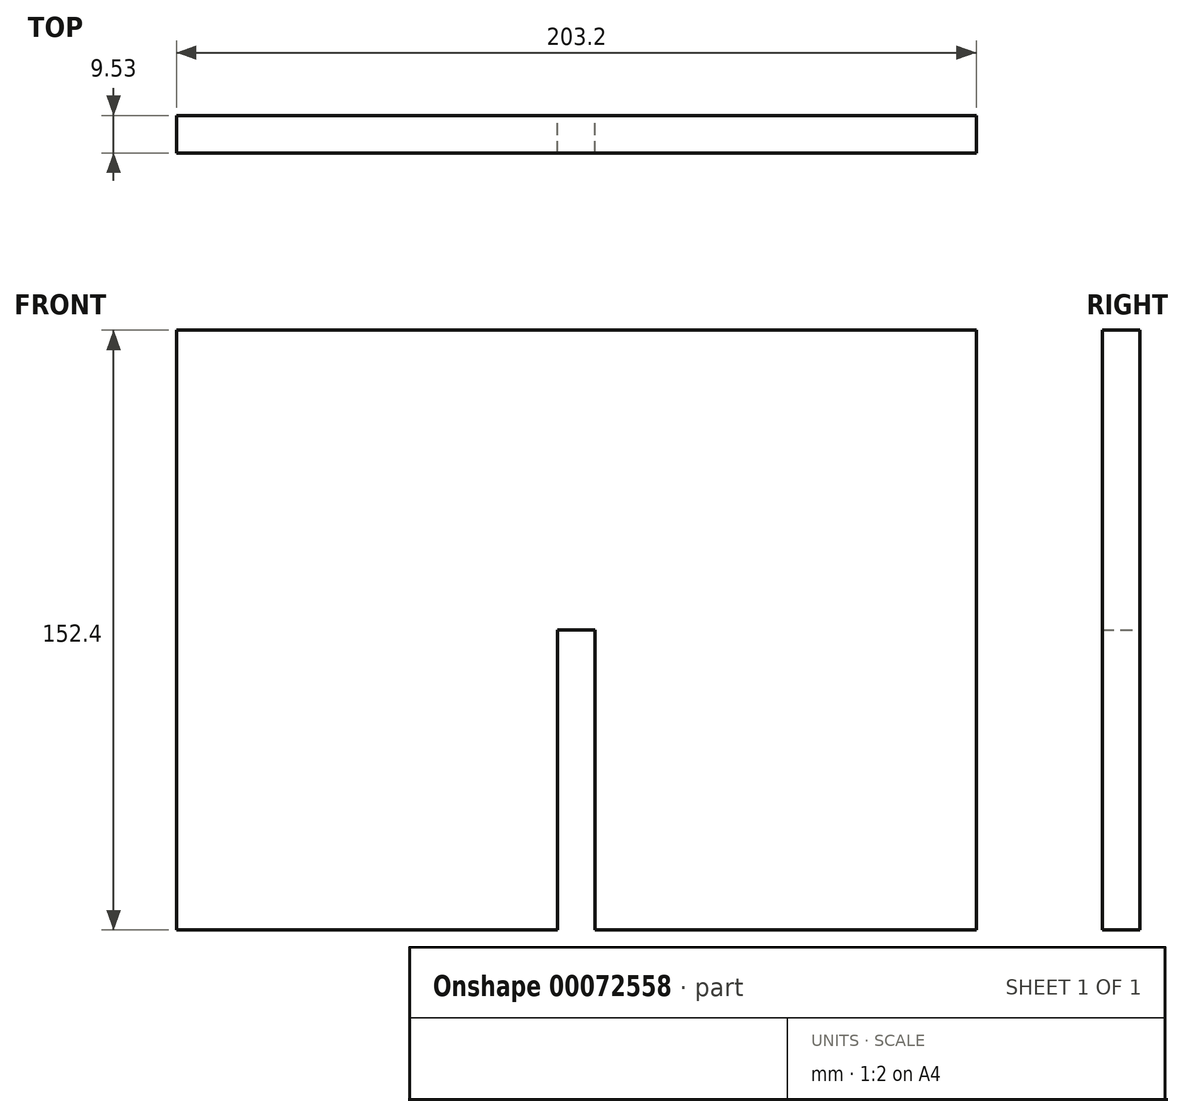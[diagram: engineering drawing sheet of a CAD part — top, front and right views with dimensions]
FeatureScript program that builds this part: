
annotation { "Feature Type Name" : "Feature", "Feature Type Description" : "" }
export const myFeature = defineFeature(function(context is Context, id is Id, definition is map)
    precondition{}
    {
        {
            var Q0;
            Q0=qCreatedBy(makeId("Front.planeOp"),FACE);
            var sketch = newSketch(context, id + "F0", { "sketchPlane" : qUnion([Q0])});
            skLineSegment(sketch, "E0.bottom", {"start": v(0, 0) * mm, "end": v(-96.84, 0) * mm});
            skLineSegment(sketch, "E0.top", {"start": v(0, 152.4) * mm, "end": v(-203.2, 152.4) * mm});
            skLineSegment(sketch, "E0.left", {"start": v(0, 0) * mm, "end": v(0, 152.4) * mm});
            skLineSegment(sketch, "E0.right", {"start": v(-203.2, 0) * mm, "end": v(-203.2, 152.4) * mm});
            skLineSegment(sketch, "E1", {"start": v(-96.84, 76.2) * mm, "end": v(-106.36, 76.2) * mm});
            skPoint(sketch, "E1.startSnap0", {"position": v(0, 76.2) * mm});
            skPoint(sketch, "E1.endSnap0", {"position": v(0, 76.2) * mm});
            skLineSegment(sketch, "E2", {"start": v(-106.36, 76.2) * mm, "end": v(-106.36, 0) * mm});
            skLineSegment(sketch, "E3", {"start": v(-96.84, 76.2) * mm, "end": v(-96.84, 0) * mm});
            skLineSegment(sketch, "E4", {"start": v(-101.6, 76.2) * mm, "end": v(-101.6, 152.4) * mm});
            skLineSegment(sketch, "E5.trimOffspring", {"start": v(-106.36, 0) * mm, "end": v(-203.2, 0) * mm});
            skSolve(sketch);
        }
        {
            var Q0;
            {var subQ3=sQuery(id+"F0.wireOp",EDGE,"E0.right");Q0=makeQuery(id+"F0.imprint","IMPRINT",FACE,{"disambiguationData":[TD([[makeQuery(id+"F0.imprint","IMPRINT",EDGE,{"derivedFrom":subQ3}),-1.0]])]});}
            var Q1;
            {var subQ3=sQuery(id+"F0.wireOp",EDGE,"E0.left");Q1=makeQuery(id+"F0.imprint","IMPRINT",FACE,{"disambiguationData":[TD([[makeQuery(id+"F0.imprint","IMPRINT",EDGE,{"derivedFrom":subQ3}),1.0]])]});}
            extrude(context, id + "F1", {"entities" : qUnion([Q0, Q1]), "depth" : 9.52 * mm});
        }
    });
